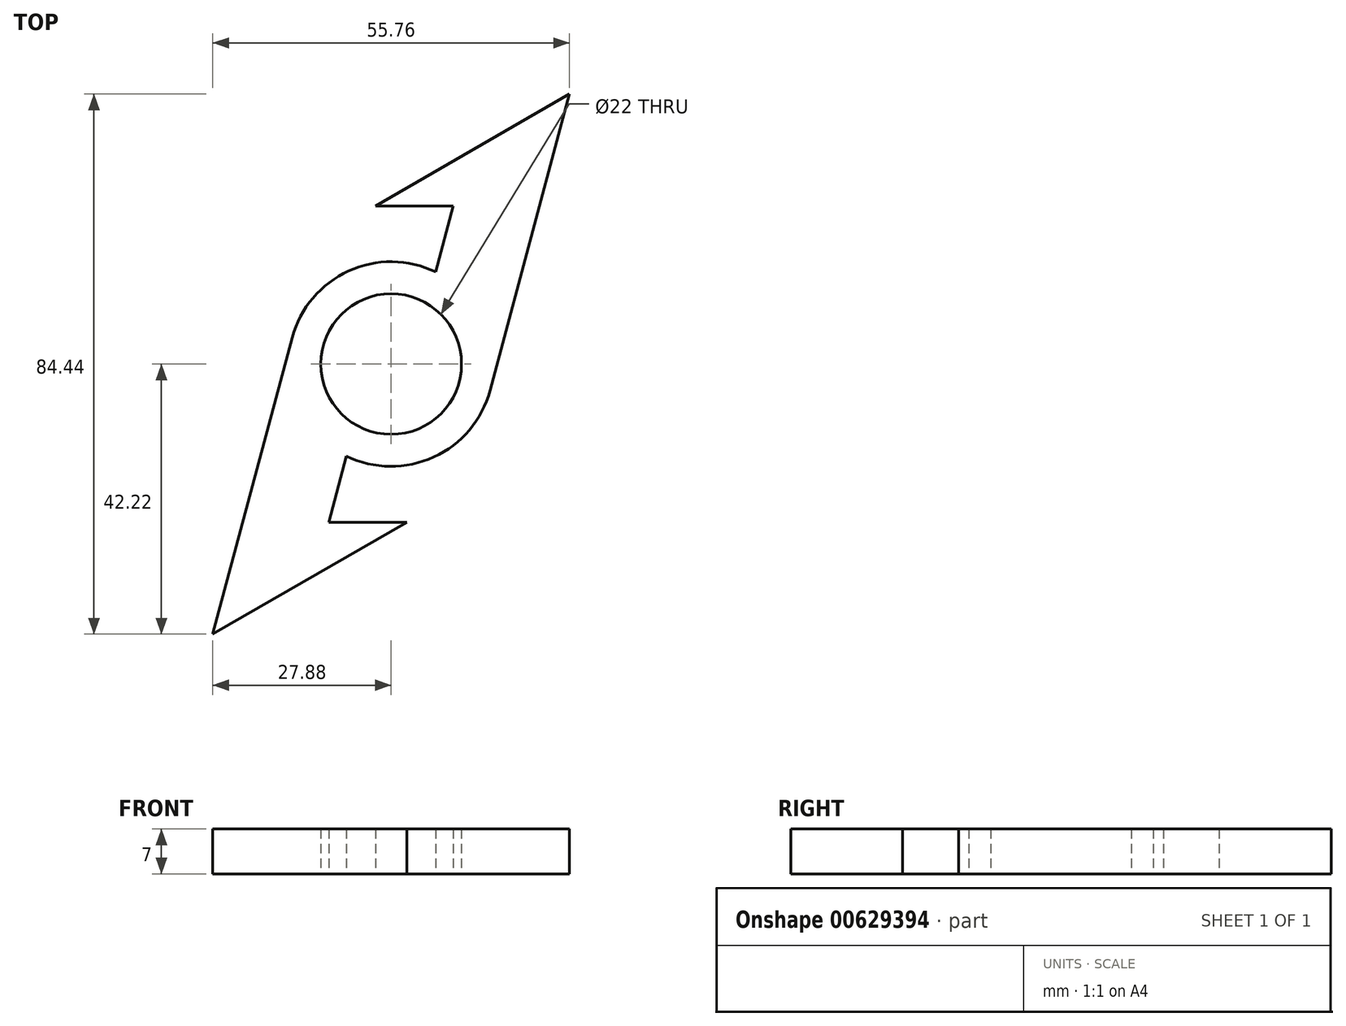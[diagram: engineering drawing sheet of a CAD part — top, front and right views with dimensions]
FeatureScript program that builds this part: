
annotation { "Feature Type Name" : "Feature", "Feature Type Description" : "" }
export const myFeature = defineFeature(function(context is Context, id is Id, definition is map)
    precondition{}
    {
        {
            var Q0;
            Q0=qCreatedBy(makeId("Top.planeOp"),FACE);
            var sketch = newSketch(context, id + "F0", { "sketchPlane" : qUnion([Q0])});
            skCircle(sketch, "E0", {"center": v(0, 0) * mm, "radius": 11 * mm});
            skCircle(sketch, "E1", {"center": v(0, 0) * mm, "radius": 16 * mm});
            skLineSegment(sketch, "E2", {"start": v(15.45, -4.14) * mm, "end": v(27.88, 42.22) * mm});
            skLineSegment(sketch, "E3", {"start": v(27.88, 42.22) * mm, "end": v(-2.43, 24.72) * mm});
            skLineSegment(sketch, "E4", {"start": v(-2.43, 24.72) * mm, "end": v(9.73, 24.72) * mm});
            skLineSegment(sketch, "E5", {"start": v(9.73, 24.72) * mm, "end": v(6.97, 14.4) * mm});
            skLineSegment(sketch, "E6.1.0", {"start": v(-9.73, -24.72) * mm, "end": v(-6.97, -14.4) * mm});
            skLineSegment(sketch, "E6.1.1", {"start": v(2.43, -24.72) * mm, "end": v(-9.73, -24.72) * mm});
            skLineSegment(sketch, "E6.1.2", {"start": v(-27.88, -42.22) * mm, "end": v(2.43, -24.72) * mm});
            skLineSegment(sketch, "E6.1.3", {"start": v(-15.45, 4.14) * mm, "end": v(-27.88, -42.22) * mm});
            skSolve(sketch);
        }
        {
            var Q0;
            Q0=makeQuery(id+"F0.imprint","IMPRINT",FACE,{"disambiguationData":[TD([[makeQuery(id+"F0.imprint","IMPRINT",EDGE,{"derivedFrom":sQuery(id+"F0.wireOp",EDGE,"E0")}),-1.0]])]});
            var Q1;
            {var subQ0=sQuery(id+"F0.wireOp",EDGE,"E2");Q1=makeQuery(id+"F0.imprint","IMPRINT",FACE,{"disambiguationData":[TD([[makeQuery(id+"F0.imprint","IMPRINT",EDGE,{"derivedFrom":subQ0}),1.0]])]});}
            var Q2;
            {var subQ0=sQuery(id+"F0.wireOp",EDGE,"E6.1.0");Q2=makeQuery(id+"F0.imprint","IMPRINT",FACE,{"disambiguationData":[TD([[makeQuery(id+"F0.imprint","IMPRINT",EDGE,{"derivedFrom":subQ0}),1.0]])]});}
            extrude(context, id + "F1", {"entities" : qUnion([Q0, Q1, Q2]), "endBound" : BoundingType.SYMMETRIC, "depth" : 7 * mm, "offsetDistance" : 25 * mm});
        }
    });
